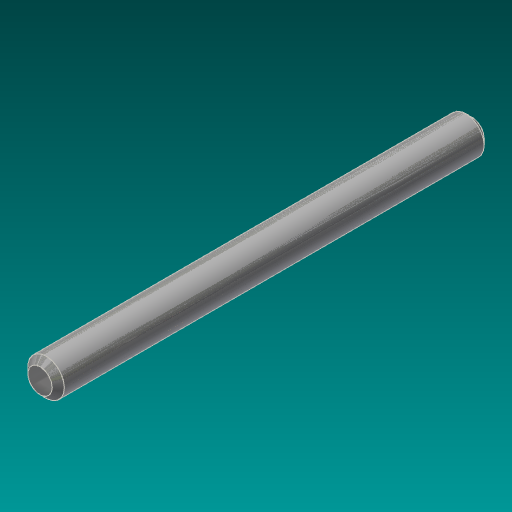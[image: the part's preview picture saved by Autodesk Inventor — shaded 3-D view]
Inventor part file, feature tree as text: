
AUTODESK INVENTOR PART (.ipt)
format: ipt  version: 2017.3 (Build 213256000, 256)  size: 112,640 bytes
history: native  units: in
note: dims shown in document units (in); Inventor stores cm internally (conversion verified against a paired STEP export)
features: extrude x1, chamfer x1, sketch x1
ambient origin geometry x8: Origin, YZ Plane, XZ Plane, XY Plane, X Axis, Y Axis, Z Axis, Center Point
bodies: Solid1 (feature_tree)
feature tree (3):
  extrude  "Extrusion1"  Depth=4.4375in TaperAngle=0.0deg
  chamfer  "Chamfer1"  Distance=0.0625in Angle=45.0deg
  sketch  "Sketch1"  dims[d0=0.375in d1=4.4375in d2=0.0in d3=0.0625in d4=0.125in d5=45.0deg]
